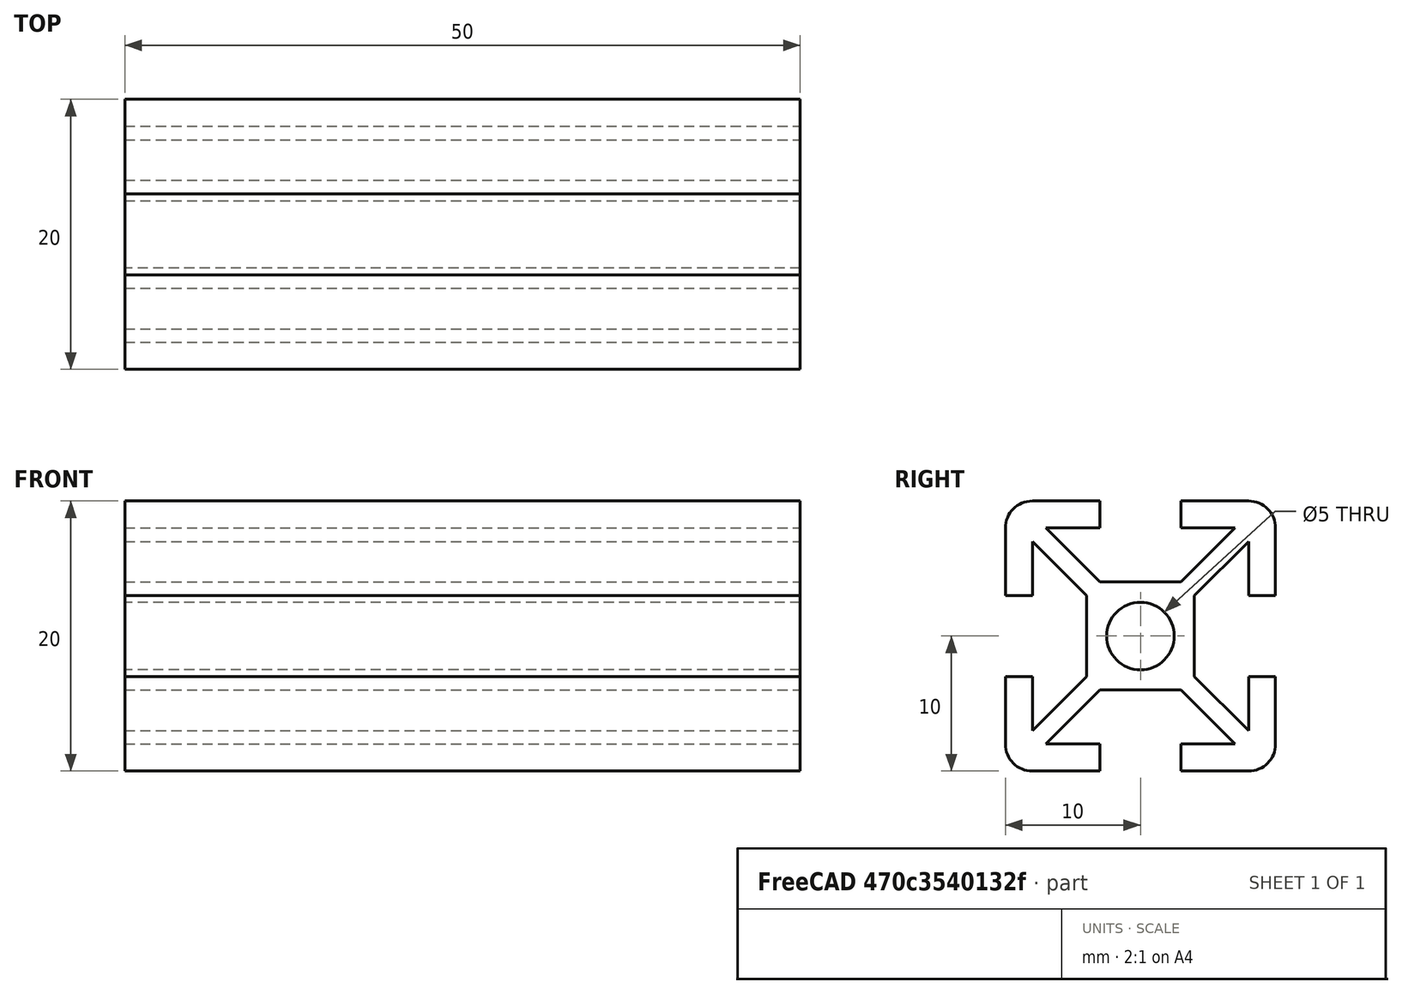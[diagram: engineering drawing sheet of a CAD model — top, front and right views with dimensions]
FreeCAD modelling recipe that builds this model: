
FCSTD DOCUMENT  (FreeCAD 0.19R24267 +99 (Git))
Label: 2020 Rail strut for feet left right 50mm
License: All rights reserved
LicenseURL: http://en.wikipedia.org/wiki/All_rights_reserved
objects: Sketcher::SketchObject×1, PartDesign::Pad×1, PartDesign::Body×1
note: 4 computed .brp shape members not serialized (recipe doc carries the construction recipe); baked Part::Feature solids carry a one-line shape summary decoded from their .brp

FEATURE [Sketcher::SketchObject] Sketch  label="Rail cross section"
  FullyConstrained = true
  MapMode = 5
  Placement = pos=(0,0,0) rot=(0.57735,0.57735,0.57735;2.0944rad)
  Support = -> [YZ_Plane]
  sketch-geometry (47):
    g0: ArcOfCircle CenterX=-8 CenterY=8 CenterZ=0 NormalX=0 NormalY=0 NormalZ=1 AngleXU=0 Radius=2 StartAngle=1.5708 EndAngle=3.14159
    g1: ArcOfCircle CenterX=-8 CenterY=-8 CenterZ=0 NormalX=0 NormalY=0 NormalZ=1 AngleXU=0 Radius=2 StartAngle=3.14159 EndAngle=4.71239
    g2: ArcOfCircle CenterX=8 CenterY=-8 CenterZ=0 NormalX=0 NormalY=0 NormalZ=1 AngleXU=0 Radius=2 StartAngle=4.71239 EndAngle=6.28319
    g3: ArcOfCircle CenterX=8 CenterY=8 CenterZ=0 NormalX=0 NormalY=0 NormalZ=1 AngleXU=0 Radius=2 StartAngle=1e-16 EndAngle=1.5708
    g4: Circle CenterX=0 CenterY=0 CenterZ=0 NormalX=0 NormalY=0 NormalZ=1 AngleXU=0 Radius=2.5
    g5: LineSegment StartX=-10 StartY=8 StartZ=0 EndX=-10 EndY=3 EndZ=0
    g6: LineSegment StartX=-10 StartY=-3 StartZ=0 EndX=-10 EndY=-8 EndZ=0
    g7: LineSegment StartX=-8 StartY=-10 StartZ=0 EndX=-3 EndY=-10 EndZ=0
    g8: LineSegment StartX=3 StartY=-10 StartZ=0 EndX=8 EndY=-10 EndZ=0
    g9: LineSegment StartX=10 StartY=-8 StartZ=0 EndX=10 EndY=-3 EndZ=0
    g10: LineSegment StartX=10 StartY=3 StartZ=0 EndX=10 EndY=8 EndZ=0
    g11: LineSegment StartX=-8 StartY=10 StartZ=0 EndX=-3 EndY=10 EndZ=0
    g12: LineSegment StartX=3 StartY=10 StartZ=0 EndX=8 EndY=10 EndZ=0
    g13: LineSegment StartX=-3 StartY=4 StartZ=0 EndX=3 EndY=4 EndZ=0
    g14: LineSegment StartX=4 StartY=3 StartZ=0 EndX=4 EndY=-3 EndZ=0
    g15: LineSegment StartX=3 StartY=-4 StartZ=0 EndX=-3 EndY=-4 EndZ=0
    g16: LineSegment StartX=-4 StartY=-3 StartZ=0 EndX=-4 EndY=3 EndZ=0
    g17: LineSegment StartX=-3 StartY=-4 StartZ=0 EndX=-7 EndY=-8 EndZ=0
    g18: LineSegment StartX=-3 StartY=-10 StartZ=0 EndX=-3 EndY=-8 EndZ=0
    g19: LineSegment StartX=3 StartY=-4 StartZ=0 EndX=7 EndY=-8 EndZ=0
    g20: LineSegment StartX=4 StartY=-3 StartZ=0 EndX=8 EndY=-7 EndZ=0
    g21: LineSegment StartX=8 StartY=-7 StartZ=0 EndX=8 EndY=-3 EndZ=0
    g22: LineSegment StartX=10 StartY=-3 StartZ=0 EndX=8 EndY=-3 EndZ=0
    g23: LineSegment StartX=4 StartY=3 StartZ=0 EndX=8 EndY=7 EndZ=0
    g24: LineSegment StartX=8 StartY=7 StartZ=0 EndX=8 EndY=3 EndZ=0
    g25: LineSegment StartX=8 StartY=3 StartZ=0 EndX=10 EndY=3 EndZ=0
    g26: LineSegment StartX=3 StartY=10 StartZ=0 EndX=3 EndY=8 EndZ=0
    g27: LineSegment StartX=3 StartY=8 StartZ=0 EndX=7 EndY=8 EndZ=0
    g28: LineSegment StartX=7 StartY=8 StartZ=0 EndX=3 EndY=4 EndZ=0
    g29: LineSegment StartX=-3 StartY=4 StartZ=0 EndX=-7 EndY=8 EndZ=0
    g30: LineSegment StartX=-7 StartY=8 StartZ=0 EndX=-3 EndY=8 EndZ=0
    g31: LineSegment StartX=-3 StartY=8 StartZ=0 EndX=-3 EndY=10 EndZ=0
    g32: LineSegment StartX=-4 StartY=3 StartZ=0 EndX=-8 EndY=7 EndZ=0
    g33: LineSegment StartX=-8 StartY=3 StartZ=0 EndX=-10 EndY=3 EndZ=0
    g34: LineSegment StartX=-10 StartY=-3 StartZ=0 EndX=-8 EndY=-3 EndZ=0
    g35: LineSegment StartX=-8 StartY=-7 StartZ=0 EndX=-4 EndY=-3 EndZ=0
    g36: LineSegment StartX=3 StartY=-10 StartZ=0 EndX=3 EndY=-8 EndZ=0
    g37: LineSegment StartX=3 StartY=-8 StartZ=0 EndX=7 EndY=-8 EndZ=0
    g38: LineSegment StartX=-3 StartY=-8 StartZ=0 EndX=-7 EndY=-8 EndZ=0
    g39: LineSegment StartX=-8 StartY=-7 StartZ=0 EndX=-8 EndY=-3 EndZ=0
    g40: LineSegment StartX=-8 StartY=3 StartZ=0 EndX=-8 EndY=7 EndZ=0
    g41: LineSegment StartX=-3 StartY=10 StartZ=0 EndX=3 EndY=10 EndZ=0
    g42: LineSegment StartX=10 StartY=3 StartZ=0 EndX=10 EndY=-3 EndZ=0
    g43: LineSegment StartX=3 StartY=-10 StartZ=0 EndX=-3 EndY=-10 EndZ=0
    g44: LineSegment StartX=-10 StartY=-3 StartZ=0 EndX=-10 EndY=3 EndZ=0
    g45: LineSegment StartX=-4 StartY=-3 StartZ=0 EndX=-3 EndY=-4 EndZ=0
    g46: LineSegment StartX=-8 StartY=-7 StartZ=0 EndX=-7 EndY=-8 EndZ=0
  constraints (128):
    c: Radius(g0) = 2  'ASSUMED EDGE RADIUS'
    c: Equal(g1,g2)
    c: Coincident(g4,g-1)
    c: Radius(g4) = 2.5  'CENTER HOLE'
    c: Vertical(g6)
    c: Horizontal(g7)
    c: Horizontal(g8)
    c: Vertical(g9)
    c: Vertical(g10)
    c: Horizontal(g11)
    c: Horizontal(g12)
    c: DistanceX(g0,g3) = 20  'RAIL WIDTH'
    c: Vertical(g5)
    c: DistanceY(g2,g3) = 20  'RAIL HEIGHT'
    c: DistanceX(g7,g8) = 6  'SLOT WIDTH'
    c: Equal(g8,g7)
    c: Equal(g7,g6)
    c: Equal(g5,g11)
    c: Equal(g12,g10)
    c: Tangent(g12,g3) = 1.5708
    c: Tangent(g10,g3) = -1.5708
    c: Tangent(g11,g0) = 1.5708
    c: Tangent(g5,g0) = -1.5708
    c: Tangent(g6,g1) = -1.5708
    c: Tangent(g7,g1) = -1.5708
    c: Tangent(g8,g2) = -1.5708
    c: Tangent(g9,g2) = -1.5708
    c: Symmetric(g3,g2,g-1)
    c: Symmetric(g0,g3,g-2)
    c: Horizontal(g13)
    c: Vertical(g14)
    c: Vertical(g16)
    c: Horizontal(g15)
    c: Equal(g16,g15)
    c: Equal(g15,g14)
    c: Coincident(g17,g15)
    c: Coincident(g18,g7)
    c: Vertical(g18)
    c: Coincident(g19,g15)
    c: Coincident(g20,g14)
    c: Coincident(g21,g20)
    c: Vertical(g21)
    c: Coincident(g22,g9)
    c: Coincident(g22,g21)
    c: Coincident(g23,g14)
    c: Coincident(g24,g23)
    c: Vertical(g24)
    c: Coincident(g25,g24)
    c: Coincident(g25,g10)
    c: Coincident(g26,g12)
    c: Vertical(g26)
    c: Coincident(g27,g26)
    c: Horizontal(g27)
    c: Coincident(g28,g27)
    c: Coincident(g28,g13)
    c: Coincident(g29,g13)
    c: Coincident(g30,g29)
    c: Horizontal(g30)
    c: Coincident(g31,g30)
    c: Coincident(g31,g11)
    c: Coincident(g32,g16)
    c: Coincident(g33,g5)
    c: Horizontal(g33)
    c: Coincident(g34,g6)
    c: Horizontal(g34)
    c: Coincident(g35,g16)
    c: Coincident(g36,g8)
    c: Vertical(g36)
    c: Coincident(g37,g36)
    c: Coincident(g37,g19)
    c: Coincident(g38,g18)
    c: Coincident(g38,g17)
    c: Horizontal(g38)
    c: Coincident(g39,g35)
    c: Coincident(g39,g34)
    c: Vertical(g39)
    c: Coincident(g40,g33)
    c: Coincident(g40,g32)
    c: Vertical(g40)
    c: Horizontal(g37)
    c: Horizontal(g25)
    c: Horizontal(g22)
    c: Equal(g38,g37)
    c: Equal(g37,g21)
    c: Equal(g21,g24)
    c: Equal(g24,g27)
    c: Equal(g27,g30)
    c: Equal(g30,g40)
    c: Equal(g40,g39)
    c: Vertical(g31)
    c: Equal(g31,g26)
    c: Equal(g26,g25)
    c: Equal(g25,g22)
    c: Equal(g22,g36)
    c: Equal(g36,g18)
    c: Equal(g18,g34)
    c: Equal(g34,g33)
    c: Equal(g32,g29)
    c: Equal(g29,g28)
    c: Equal(g28,g23)
    c: Equal(g23,g20)
    c: Equal(g20,g19)
    c: Equal(g19,g17)
    c: Equal(g17,g35)
    c: Coincident(g41,g11)
    c: Coincident(g41,g12)
    c: Coincident(g42,g10)
    c: Coincident(g42,g9)
    c: Coincident(g43,g8)
    c: Coincident(g43,g7)
    c: Horizontal(g43)
    c: Coincident(g44,g6)
    c: Coincident(g44,g5)
    c: Vertical(g44)
    c: Horizontal(g41)
    c: DistanceY(g8,g15) = 6  'ASSUMED SLOT DEPTH'
    c: Equal(g43,g15)
    c: Equal(g16,g13)
    c: Equal(g44,g43)
    c: Equal(g43,g42)
    c: Equal(g42,g41)
    c: Vertical(g42)
    c: DistanceY(g36,g36) = 2  'ASSUMED WALL THICKNESS'
    c: Coincident(g45,g16)
    c: Coincident(g45,g15)
    c: Coincident(g46,g35)
    c: Coincident(g46,g17)
    c: Equal(g45,g46)
FEATURE [PartDesign::Pad] Pad  label="Length"
  Direction = (1,1,1)
  Length = 50
  Length2 = 100
  Placement = pos=(0,0,0) rot=(0.57735,0.57735,0.57735;2.0944rad)
  Profile = -> Sketch
  Type = 0
FEATURE [PartDesign::Body] Body
  Group = -> [Sketch,Pad]
  Origin = -> Origin
  Tip = -> Pad
